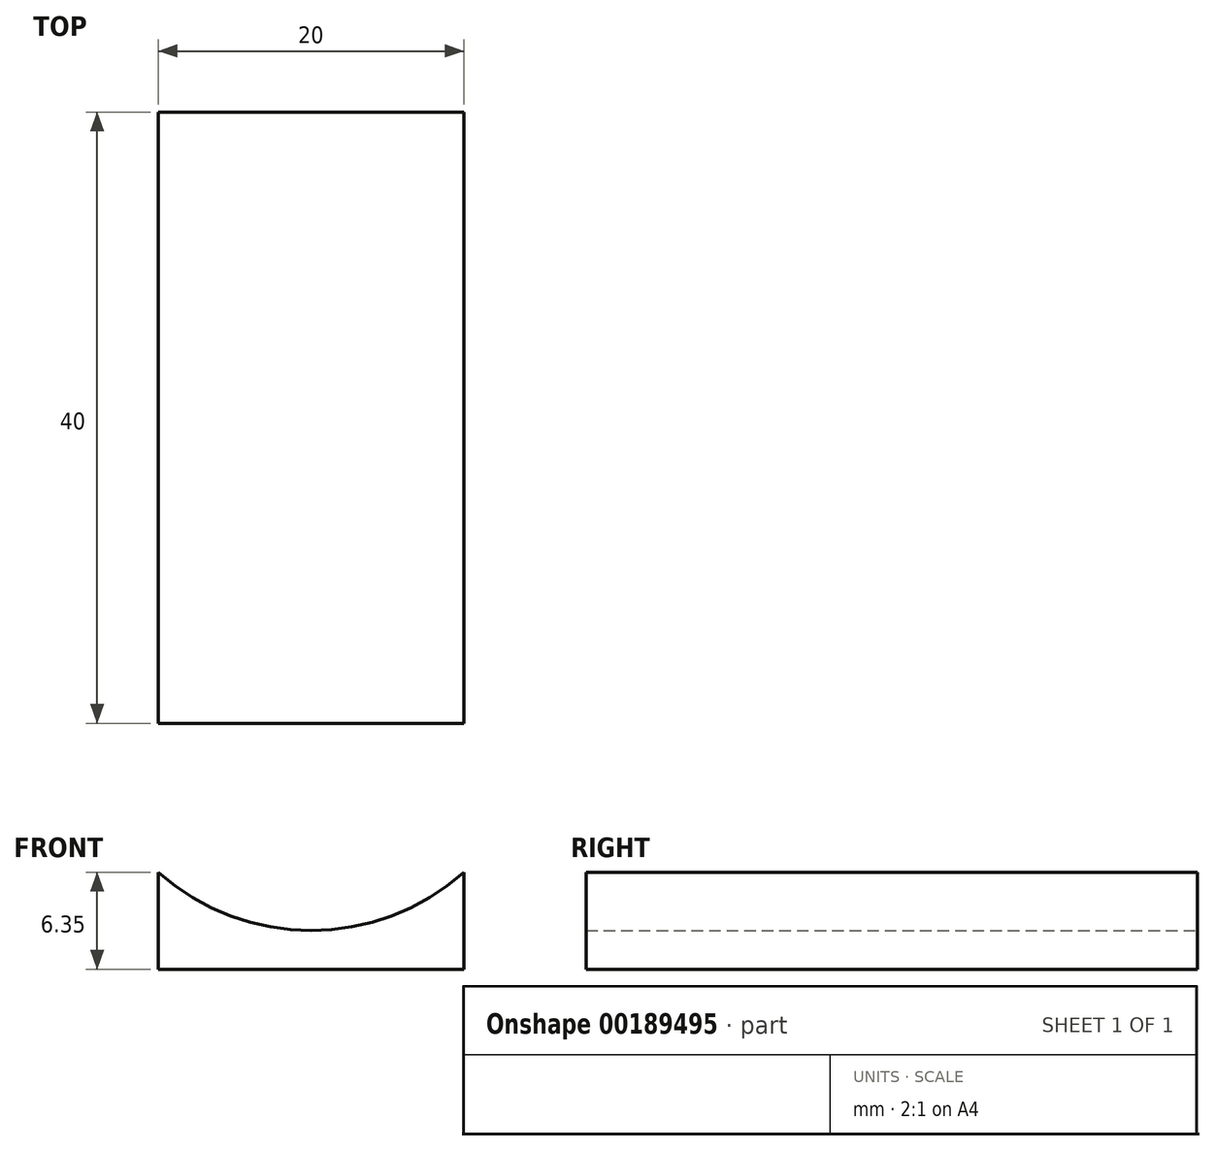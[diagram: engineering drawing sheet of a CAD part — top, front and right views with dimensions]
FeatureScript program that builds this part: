
annotation { "Feature Type Name" : "Feature", "Feature Type Description" : "" }
export const myFeature = defineFeature(function(context is Context, id is Id, definition is map)
    precondition{}
    {
        {
            var Q0;
            Q0=qCreatedBy(makeId("Front.planeOp"),FACE);
            var sketch = newSketch(context, id + "F0", { "sketchPlane" : qUnion([Q0])});
            skArc(sketch, "E0", {"start": v(-10, -11.18) * mm, "mid": v(0, -15) * mm, "end": v(10, -11.18) * mm});
            skLineSegment(sketch, "E1.top", {"start": v(0, -17.53) * mm, "end": v(10, -17.53) * mm});
            skLineSegment(sketch, "E1.right", {"start": v(10, -11.18) * mm, "end": v(10, -17.53) * mm});
            skLineSegment(sketch, "E2.top", {"start": v(0, -17.53) * mm, "end": v(-10, -17.53) * mm});
            skLineSegment(sketch, "E2.right", {"start": v(-10, -11.18) * mm, "end": v(-10, -17.53) * mm});
            skSolve(sketch);
        }
        {
            var Q0;
            Q0=makeQuery(id+"F0.imprint","IMPRINT",FACE,{"disambiguationData":[TD([[makeQuery(id+"F0.imprint","IMPRINT",EDGE,{"derivedFrom":sQuery(id+"F0.wireOp",EDGE,"E0")}),-1.0]])]});
            extrude(context, id + "F1", {"entities" : qUnion([Q0]), "depth" : 40 * mm});
        }
    });
